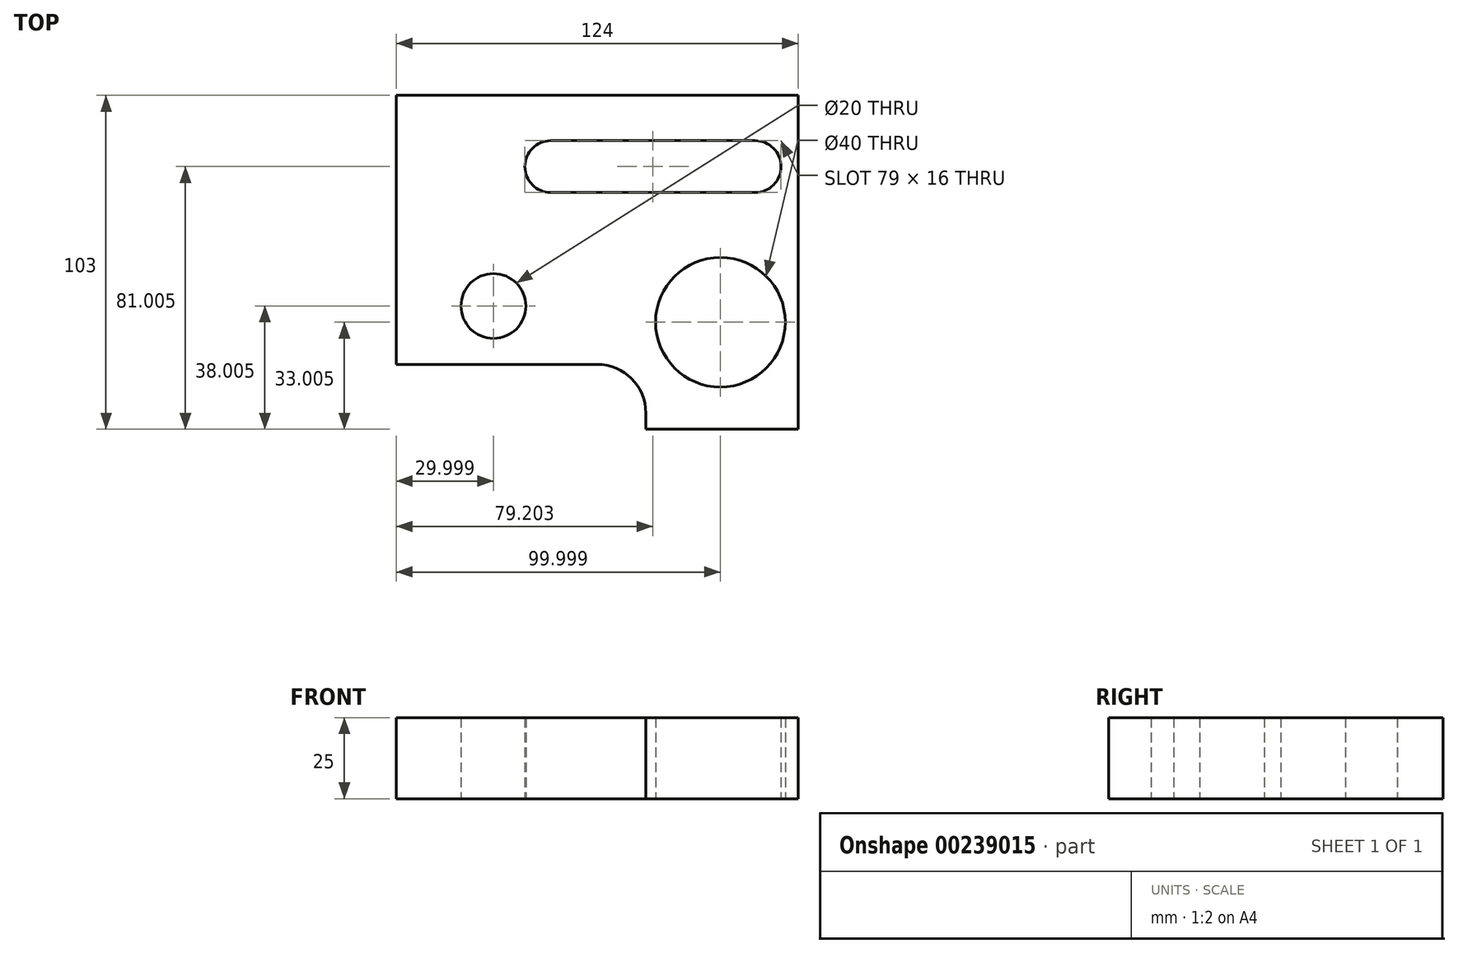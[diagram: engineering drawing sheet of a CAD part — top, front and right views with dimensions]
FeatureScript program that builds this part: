
annotation { "Feature Type Name" : "Feature", "Feature Type Description" : "" }
export const myFeature = defineFeature(function(context is Context, id is Id, definition is map)
    precondition{}
    {
        {
            var Q0;
            Q0=qCreatedBy(makeId("Top.planeOp"),FACE);
            var sketch = newSketch(context, id + "F0", { "sketchPlane" : qUnion([Q0])});
            skLineSegment(sketch, "E0", {"start": v(68.49, -51.9) * mm, "end": v(68.49, 51.1) * mm});
            skLineSegment(sketch, "E1", {"start": v(68.49, 51.1) * mm, "end": v(-55.51, 51.1) * mm});
            skLineSegment(sketch, "E2", {"start": v(-55.51, 51.1) * mm, "end": v(-55.51, -31.9) * mm});
            skLineSegment(sketch, "E3", {"start": v(-55.51, -31.9) * mm, "end": v(6.49, -31.9) * mm});
            skLineSegment(sketch, "E4", {"start": v(68.49, -51.9) * mm, "end": v(21.49, -51.9) * mm});
            skLineSegment(sketch, "E5", {"start": v(21.49, -46.9) * mm, "end": v(21.49, -51.9) * mm});
            skLineSegment(sketch, "E6", {"start": v(-55.51, -31.9) * mm, "end": v(-25.51, -31.9) * mm});
            skLineSegment(sketch, "E7", {"start": v(-25.51, -31.9) * mm, "end": v(-25.51, -13.9) * mm});
            skCircle(sketch, "E8", {"center": v(-25.51, -13.9) * mm, "radius": 10 * mm});
            skPoint(sketch, "E9.visualSharp", {"position": v(21.49, -31.9) * mm});
            skArc(sketch, "E9.filletArc", {"start": v(21.49, -46.9) * mm, "mid": v(17.1, -36.29) * mm, "end": v(6.49, -31.9) * mm});
            skLineSegment(sketch, "E10", {"start": v(68.49, -51.9) * mm, "end": v(68.49, -18.9) * mm});
            skLineSegment(sketch, "E11", {"start": v(68.49, -18.9) * mm, "end": v(44.49, -18.9) * mm});
            skCircle(sketch, "E12", {"center": v(44.49, -18.9) * mm, "radius": 20 * mm});
            skLineSegment(sketch, "E13", {"start": v(68.49, 51.1) * mm, "end": v(63.2, 51.1) * mm});
            skLineSegment(sketch, "E14", {"start": v(63.2, 51.1) * mm, "end": v(63.2, 37.1) * mm, "construction": true});
            skLineSegment(sketch, "E15", {"start": v(63.2, 29.1) * mm, "end": v(63.2, 29.1) * mm});
            skLineSegment(sketch, "E16", {"start": v(55.2, 21.1) * mm, "end": v(-7.8, 21.1) * mm});
            skLineSegment(sketch, "E17", {"start": v(-15.8, 29.1) * mm, "end": v(-15.8, 29.1) * mm});
            skLineSegment(sketch, "E18", {"start": v(55.2, 37.1) * mm, "end": v(-7.8, 37.1) * mm});
            skPoint(sketch, "E19.visualSharp", {"position": v(-15.8, 37.1) * mm});
            skArc(sketch, "E19.filletArc", {"start": v(-7.8, 37.1) * mm, "mid": v(-13.46, 34.76) * mm, "end": v(-15.8, 29.1) * mm});
            skPoint(sketch, "E20.visualSharp", {"position": v(-15.8, 21.1) * mm});
            skArc(sketch, "E20.filletArc", {"start": v(-15.8, 29.1) * mm, "mid": v(-13.46, 23.45) * mm, "end": v(-7.8, 21.1) * mm});
            skPoint(sketch, "E21.visualSharp", {"position": v(63.2, 37.1) * mm});
            skArc(sketch, "E21.filletArc", {"start": v(63.2, 29.1) * mm, "mid": v(60.85, 34.76) * mm, "end": v(55.2, 37.1) * mm});
            skPoint(sketch, "E22.visualSharp", {"position": v(63.2, 21.1) * mm});
            skArc(sketch, "E22.filletArc", {"start": v(55.2, 21.1) * mm, "mid": v(60.85, 23.45) * mm, "end": v(63.2, 29.1) * mm});
            skSolve(sketch);
        }
        {
            var Q0;
            Q0 = qSketchRegion(id + "F0", true);
            extrude(context, id + "F1", {"entities" : qUnion([Q0]), "depth" : 25 * mm});
        }
    });
